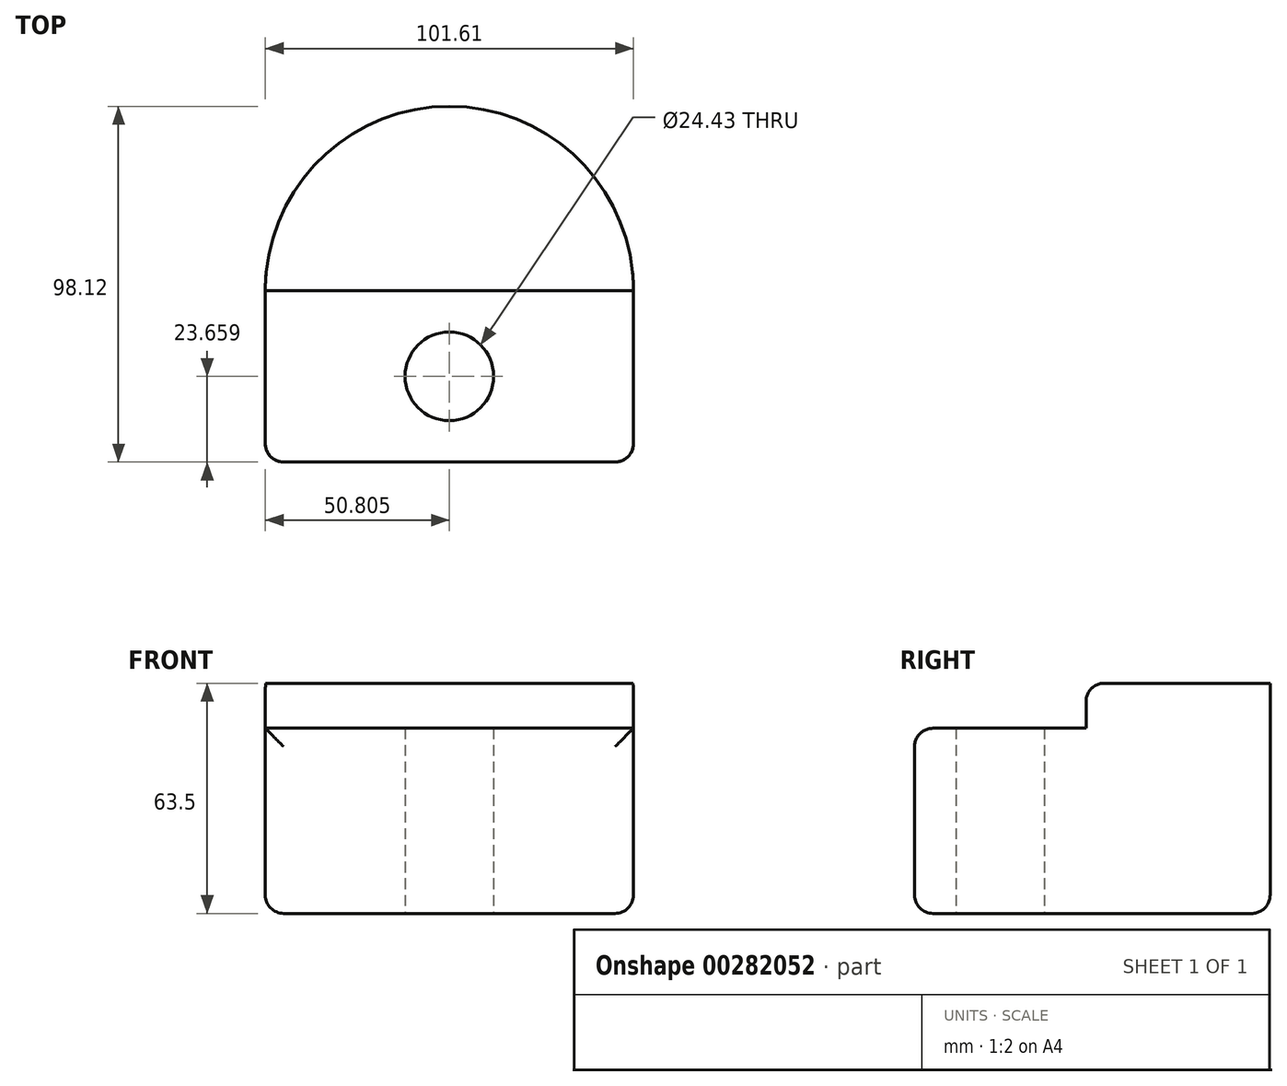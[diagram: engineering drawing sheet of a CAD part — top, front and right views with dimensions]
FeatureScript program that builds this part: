
annotation { "Feature Type Name" : "Feature", "Feature Type Description" : "" }
export const myFeature = defineFeature(function(context is Context, id is Id, definition is map)
    precondition{}
    {
        {
            var Q0;
            Q0=qCreatedBy(makeId("Top.planeOp"),FACE);
            var sketch = newSketch(context, id + "F0", { "sketchPlane" : qUnion([Q0])});
            skLineSegment(sketch, "E0", {"start": v(-74.75, -62.03) * mm, "end": v(26.85, -62.03) * mm});
            skLineSegment(sketch, "E1", {"start": v(-74.75, -14.71) * mm, "end": v(-74.75, -62.03) * mm});
            skLineSegment(sketch, "E2", {"start": v(26.85, -14.71) * mm, "end": v(26.85, -62.03) * mm});
            skArc(sketch, "E3", {"start": v(26.85, -14.71) * mm, "mid": v(-23.95, 36.09) * mm, "end": v(-74.75, -14.71) * mm});
            skLineSegment(sketch, "E4", {"start": v(-74.75, -14.71) * mm, "end": v(26.85, -14.71) * mm});
            skCircle(sketch, "E5", {"center": v(-23.95, -38.37) * mm, "radius": 12.22 * mm});
            skLineSegment(sketch, "E6", {"start": v(-74.75, -20.43) * mm, "end": v(26.85, -20.43) * mm});
            skLineSegment(sketch, "E7", {"start": v(-74.43, -9) * mm, "end": v(26.52, -9) * mm});
            skLineSegment(sketch, "E8", {"start": v(-74.75, -56.32) * mm, "end": v(26.85, -56.32) * mm});
            skSolve(sketch);
        }
        {
            var Q0;
            Q0=makeQuery(id+"F0.imprint","IMPRINT",FACE,{"disambiguationData":[TD([[makeQuery(id+"F0.imprint","IMPRINT",EDGE,{"derivedFrom":sQuery(id+"F0.wireOp",EDGE,"E5")}),-1.0]])]});
            var Q1;
            {var subQ0=sQuery(id+"F0.wireOp",EDGE,"E4");Q1=makeQuery(id+"F0.imprint","IMPRINT",FACE,{"disambiguationData":[TD([[makeQuery(id+"F0.imprint","IMPRINT",EDGE,{"derivedFrom":subQ0}),-1.0]])]});}
            var Q2;
            {var subQ0=sQuery(id+"F0.wireOp",EDGE,"E0");Q2=makeQuery(id+"F0.imprint","IMPRINT",FACE,{"disambiguationData":[TD([[makeQuery(id+"F0.imprint","IMPRINT",EDGE,{"derivedFrom":subQ0}),1.0]])]});}
            extrude(context, id + "F1", {"entities" : qUnion([Q0, Q1, Q2]), "depth" : 51.08 * mm});
        }
        {
            var Q0;
            {var subQ0=sQuery(id+"F0.wireOp",EDGE,"E7");Q0=makeQuery(id+"F0.imprint","IMPRINT",FACE,{"disambiguationData":[TD([[makeQuery(id+"F0.imprint","IMPRINT",EDGE,{"derivedFrom":subQ0}),1.0]])]});}
            var Q1;
            {var subQ0=sQuery(id+"F0.wireOp",EDGE,"E4");Q1=makeQuery(id+"F0.imprint","IMPRINT",FACE,{"disambiguationData":[TD([[makeQuery(id+"F0.imprint","IMPRINT",EDGE,{"derivedFrom":subQ0}),1.0]])]});}
            extrude(context, id + "F2", {"entities" : qUnion([Q0, Q1]), "operationType" : NewBodyOperationType.ADD, "depth" : 63.5 * mm});
        }
        {
            var Q0;
            Q0=makeQuery(id+"F1.opExtrude","CAP_EDGE",EDGE,{"disambiguationData":[OSD([sQuery(id+"F0.wireOp",EDGE,"E0")])],"isStart":false});
            var Q1;
            Q1=makeQuery(id+"F1.opExtrude","CAP_EDGE",EDGE,{"disambiguationData":[OSD([sQuery(id+"F0.wireOp",EDGE,"E4")])],"isStart":false});
            var Q2;
            Q2=makeQuery(id+"F2.opExtrude","CAP_EDGE",EDGE,{"disambiguationData":[OSD([sQuery(id+"F0.wireOp",EDGE,"E4")])],"isStart":false});
            var Q3;
            Q3=makeQuery(id+"F1.opExtrude","SWEPT_EDGE",EDGE,{"disambiguationData":[OSD([sQuery(id+"F0.wireOp",EDGE,"E0"),sQuery(id+"F0.wireOp",EDGE,"E2")])]});
            var Q4;
            Q4=makeQuery(id+"F1.opExtrude","SWEPT_EDGE",EDGE,{"disambiguationData":[OSD([sQuery(id+"F0.wireOp",EDGE,"E0"),sQuery(id+"F0.wireOp",EDGE,"E1")])]});
            var Q5;
            Q5=makeQuery(id+"F1.opExtrude","CAP_EDGE",EDGE,{"disambiguationData":[OSD([sQuery(id+"F0.wireOp",EDGE,"E0")])],"isStart":true});
            var Q6;
            Q6=makeQuery(id+"F1.opExtrude","CAP_EDGE",EDGE,{"disambiguationData":[OSD([sQuery(id+"F0.wireOp",EDGE,"E2")])],"isStart":true});
            fillet(context, id + "F3", {"entities" : qUnion([Q0, Q1, Q2, Q3, Q4, Q5, Q6]), "radius" : 5.08 * mm, "tangentPropagation" : true, "allowEdgeOverflow" : false});
        }
    });
